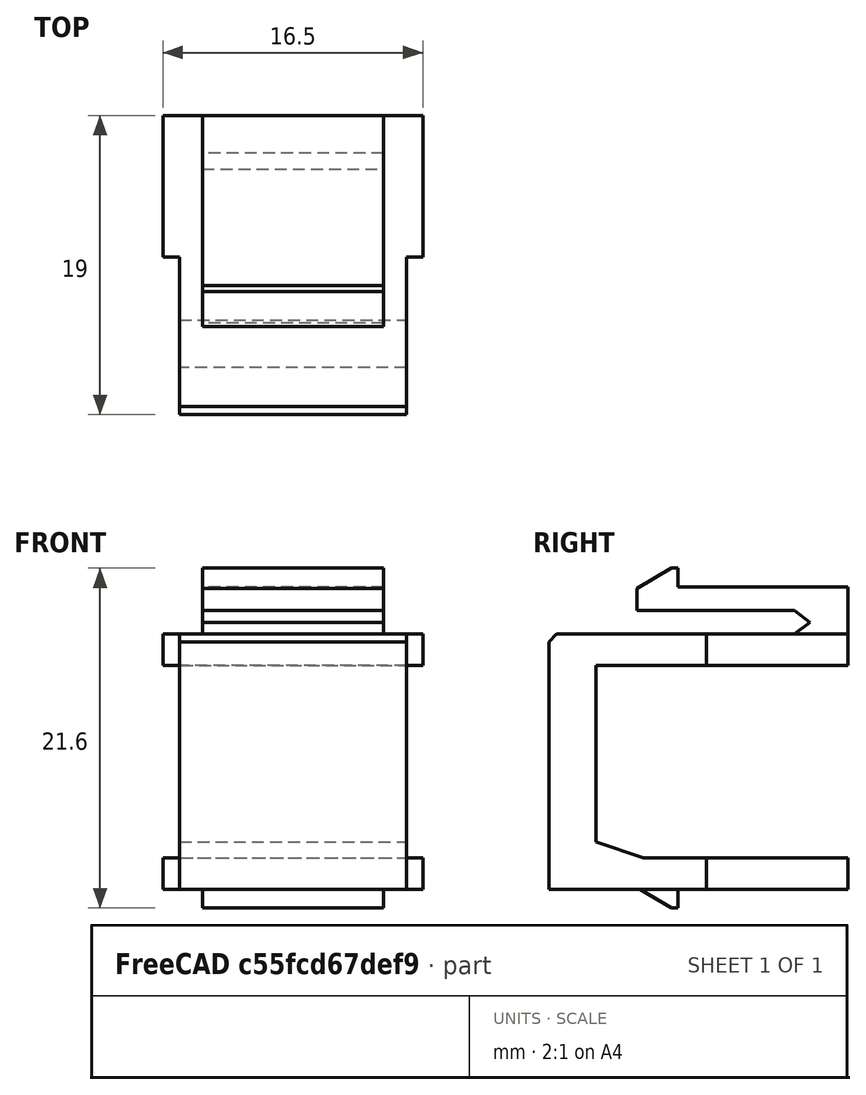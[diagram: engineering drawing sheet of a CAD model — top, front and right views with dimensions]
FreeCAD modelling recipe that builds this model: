
FCSTD DOCUMENT  (FreeCAD 1.0R39319 (Git))
Label: Blank_Keystone
License: All rights reserved
LicenseURL: https://en.wikipedia.org/wiki/All_rights_reserved
objects: Part::Feature×1, PartDesign::FeatureBase×1, PartDesign::Body×1, App::Part×1, App::FeaturePython×1, Assembly::JointGroup×1, Assembly::AssemblyObject×1
note: 4 computed .brp shape members not serialized (recipe doc carries the construction recipe); baked Part::Feature solids carry a one-line shape summary decoded from their .brp

FEATURE [Part::Feature] keystone_blank_insert_chamfer002_solid  label="keystone_blank_insert_chamfer002 (Solid)"
  shape: bbox 16.5 x 19 x 21.6 mm, 39 faces (baked)
FEATURE [PartDesign::FeatureBase] BaseFeature
  BaseFeature = -> keystone_blank_insert_chamfer002_solid
  Suppressed = false
FEATURE [PartDesign::Body] Body
  AllowCompound = false
  BaseFeature = -> keystone_blank_insert_chamfer002_solid
  Group = -> [BaseFeature]
  Origin = -> Origin
  Tip = -> BaseFeature
FEATURE [App::Part] Part  label="Keystone"
  Group = -> [keystone_blank_insert_chamfer002_solid,Body]
  Origin = -> Origin001
FEATURE [App::FeaturePython] GroundedJoint  # Assembly grounded joint (typed FeaturePython)
  ObjectToGround = -> Part
FEATURE [Assembly::JointGroup] Joints
  Group = -> [GroundedJoint]
FEATURE [Assembly::AssemblyObject] Assembly  label="Blank Keystone"
  Group = -> [Joints,Part,GroundedJoint]
  Origin = -> Origin004
  Type = Assembly
